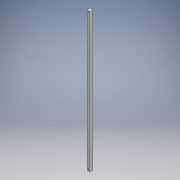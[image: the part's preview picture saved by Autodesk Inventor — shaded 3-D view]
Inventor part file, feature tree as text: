
AUTODESK INVENTOR PART (.ipt)
format: ipt  version: 2018 (Build 220112000, 112)  size: 102,912 bytes
history: native  units: mm
features: sketch x2, extrude x1, hole x1
ambient origin geometry x8: Origin, YZ Plane, XZ Plane, XY Plane, X Axis, Y Axis, Z Axis, Center Point
bodies: Body1 (feature_tree)
feature tree (4):
  extrude  "押し出し2"  Depth=30.0mm
  hole  "穴2"  [1 undecoded]
  sketch  "スケッチ4"
  sketch  "スケッチ5"
note: 1 required parameter value undecoded (feature->parameter linkage not recoverable at this tier; creation-order binding heuristic only, values carry confidence <= 0.55)
